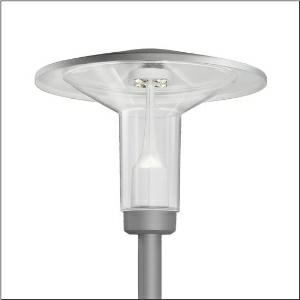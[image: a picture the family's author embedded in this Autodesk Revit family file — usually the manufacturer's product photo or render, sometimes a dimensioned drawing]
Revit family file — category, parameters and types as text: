
# Revit family: laterne_iq___p1_0a_5xa5255lf14hp_8b06
name_source: partatom
category: Lighting Fixtures
units: mm (PartAtom-declared; Revit-internal decimal feet)

## family parameters
Cut with Voids When Loaded = No
Host = Face
Light Source = No
Part Type = Normal
Room Calculation Point = No
Round Connector Dimension = Use Diameter
Shared = No

## types (1)
- --- (1 x LED, 4910 lm, 33.6 W, 4000K)
    Apparent Load = 34 VA
    CIE Flux Codes = 34 64 92 97 100
    Color Rendering = 70
    Color Temperature = 4000K
    Default Elevation = 1800 mm
    Description = Lantern iQ, mast luminaire, Module 540 iQ-SR, primary light control with 3 zone facetted reflector, of plastic, silver coated, highly specular, structured, primary optical cover: cover, of PMMA, transparent, light distribution: P1.0a, light emission: direct distribution, primary light characteristic: strongly asymmetric, installation type: post-top, LED, High Power LED, rated luminous flux: 4.910lm, luminous efficacy: 146lm/W, light colour: 740, colour temperature: 4000K, control gear: iQ Street-Remote, control: pre-setting: logarithmic dimming characteristic, Street-Remote, Auto-Match, Temp-Guard, Lumen-Switch, Night-Set, Smart-Wire, Light-Fading, Desk-Remote (wireless, voltage-free reading and setting of iQ features in the workshop via application-optimized NFC function/RFID function), optimised constant luminous flux control (CLO 2.0), with terminal, 6-pole, max. 2.5mm², mains connection: 230..240V, AC, 50/60Hz, start of lifetime: 34W, end of service life: 36W, reduction: 15W, luminaire housing, upper part, of glass-fibre reinforced polyester, coated, Siteco® metallic grey (DB 702S), diameter: 750mm, height: 583mm, spigot size: d x l = 76 x 70mm (post-top) | with reducer (optional accessory) 60 x 70mm, mounting height: 3..5m, post-top mast mounting element, of diecast aluminium, coated, Siteco® metallic grey (DB 702S), Module 540 iQ-SR, traffic white (RAL 9016), equipment: Power, protection rating (complete): IP65, insulation class (complete): insulation class II (safety insulation), certification: CE, ENEC, VDE, packaging unit: 1 piece

Light Distribution: P1.0a
    Height = 583 mm
    Lamp = 1 x LED
    Lamp Light Flux = 4910 lm
    Lamp Power = 33.6 W
    Lamp count = 1
    Length = 750 mm
    Luminous efficacy = 146 lm/W
    Manufacturer = Siteco
    ModVariant = No
    Model = 5XA5255LF14HP
    Number of Poles = 1
    OnlyDefault = Yes
    Power Factor = 1
    Product Name = Laterne iQ | P1.0a
    Product group = mast luminaire | pylon top
    ProductGroupID = 6100
    Protection Class = Protection class II
    Protection Degree = IP 65
    RLX_Detail_Level = 1
    RLX_Emergency_Light_Flux = 0 lm
    RLX_Emergency_Type = 0
    RLX_Emergency_Type_DB = No
    RlxData = <blob elided: 34489 chars, md5=9fe67129>
    Socket = socket
    Standby Power = 0 W
    System Light Flux = 4910 lm
    System Power = 34 W
    Type Comments = factory setting: luminous flux: 100 % | dim-lin: 254 | 695 mA
    Type Image = l_1006050.jpg
    URL = http://relux.com
    VarID = @adj_214655
    Voltage = 0 V
    Weight = 0.00 kg
    Width = 0 mm  [stored 0 ft]

note: [stored X ft] marks values corroborated as IEEE doubles in the binary element streams (Revit-internal decimal feet)

## geometry (parser evidence)
native form markers: Blend x4, Sweep x10
no freeform markers — native parametric forms only
